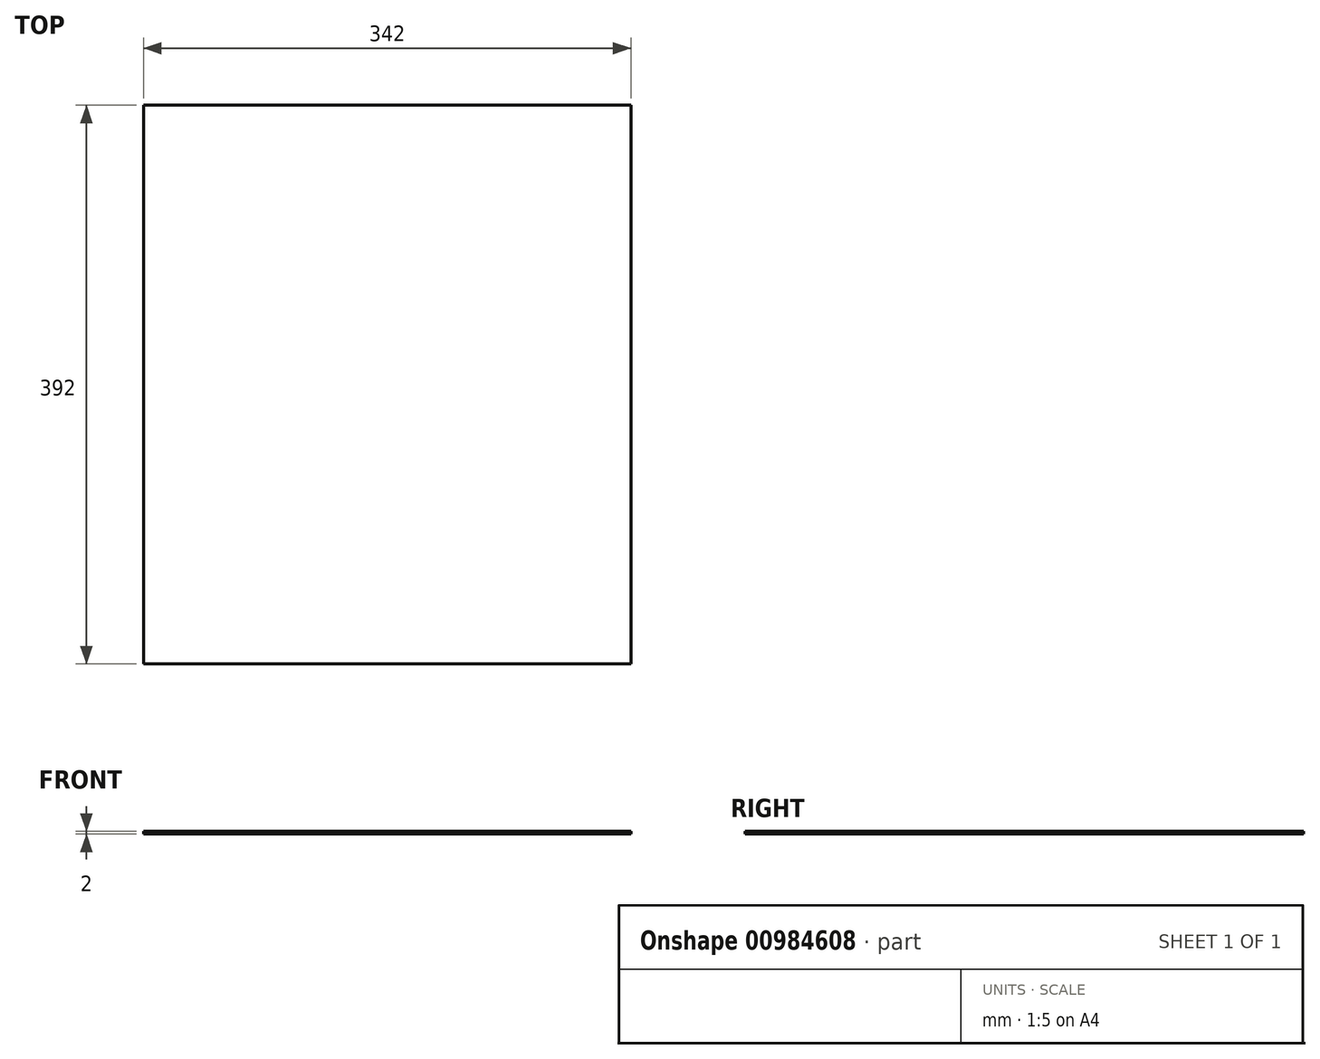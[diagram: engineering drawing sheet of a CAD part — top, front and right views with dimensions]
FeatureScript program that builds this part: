
annotation { "Feature Type Name" : "Feature", "Feature Type Description" : "" }
export const myFeature = defineFeature(function(context is Context, id is Id, definition is map)
    precondition{}
    {
        {
            var Q0;
            Q0=qCreatedBy(makeId("Top.planeOp"),FACE);
            var sketch = newSketch(context, id + "F0", { "sketchPlane" : qUnion([Q0])});
            skLineSegment(sketch, "E0.bottom", {"start": v(171, 196) * mm, "end": v(-171, 196) * mm});
            skLineSegment(sketch, "E0.top", {"start": v(171, -196) * mm, "end": v(-171, -196) * mm});
            skLineSegment(sketch, "E0.left", {"start": v(171, 196) * mm, "end": v(171, -196) * mm});
            skLineSegment(sketch, "E0.right", {"start": v(-171, 196) * mm, "end": v(-171, -196) * mm});
            skPoint(sketch, "E0.middle", {"position": v(0, 0) * mm});
            skSolve(sketch);
        }
        {
            var Q0;
            Q0=makeQuery(id+"F0.imprint","IMPRINT",FACE,{"disambiguationData":[TD([[makeQuery(id+"F0.imprint","IMPRINT",EDGE,{"derivedFrom":sQuery(id+"F0.wireOp",EDGE,"E0.bottom")}),1.0]])]});
            extrude(context, id + "F1", {"entities" : qUnion([Q0]), "depth" : 2 * mm, "offsetDistance" : 25 * mm});
        }
    });
